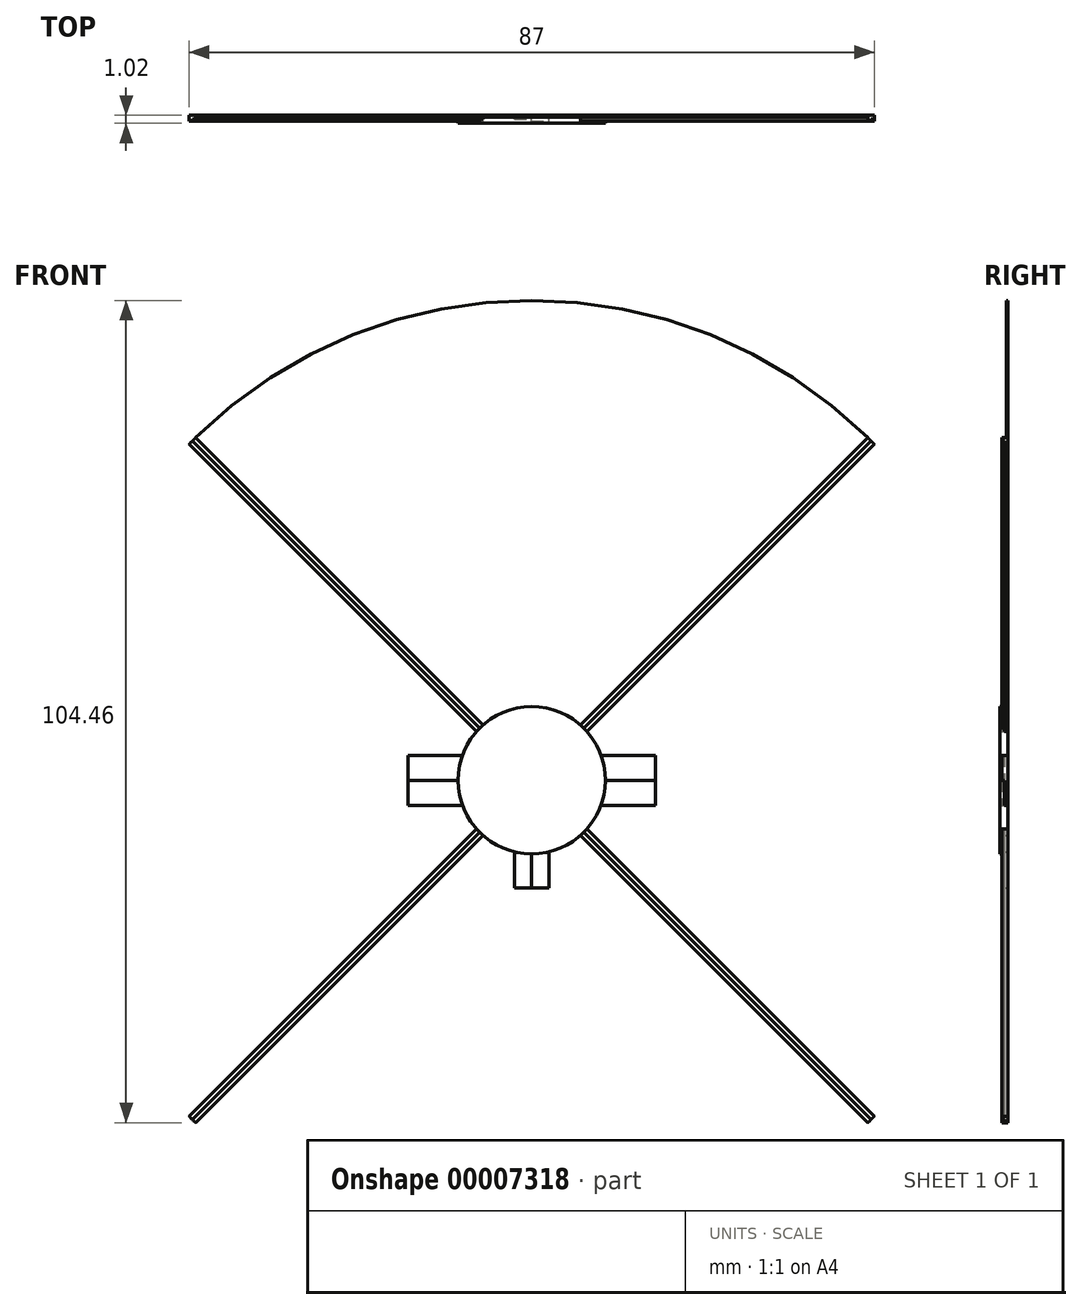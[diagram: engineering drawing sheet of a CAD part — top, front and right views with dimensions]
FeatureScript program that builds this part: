
annotation { "Feature Type Name" : "Feature", "Feature Type Description" : "" }
export const myFeature = defineFeature(function(context is Context, id is Id, definition is map)
    precondition{}
    {
        {
            var Q0;
            Q0=qCreatedBy(makeId("Front.planeOp"),FACE);
            var sketch = newSketch(context, id + "F0", { "sketchPlane" : qUnion([Q0])});
            skCircle(sketch, "E0", {"center": v(0, 0) * mm, "radius": 60.96 * mm});
            skCircle(sketch, "E1", {"center": v(0, 0) * mm, "radius": 9.35 * mm});
            skLineSegment(sketch, "E2", {"start": v(0, 0) * mm, "end": v(0, -9.35) * mm});
            skLineSegment(sketch, "E3", {"start": v(0, -9.35) * mm, "end": v(0, -60.96) * mm});
            skCircle(sketch, "E4", {"center": v(0, -11.52) * mm, "radius": 2.17 * mm});
            skLineSegment(sketch, "E5", {"start": v(-2.17, -13.7) * mm, "end": v(0, -13.7) * mm});
            skLineSegment(sketch, "E6", {"start": v(0, -13.7) * mm, "end": v(2.17, -13.7) * mm});
            skLineSegment(sketch, "E7", {"start": v(2.17, -13.7) * mm, "end": v(2.17, -9.1) * mm});
            skLineSegment(sketch, "E8", {"start": v(-2.17, -9.1) * mm, "end": v(-2.17, -13.7) * mm});
            skLineSegment(sketch, "E9", {"start": v(-8.8, 3.17) * mm, "end": v(-15.7, 3.17) * mm});
            skLineSegment(sketch, "E10", {"start": v(-15.7, 3.17) * mm, "end": v(-15.7, 0) * mm});
            skLineSegment(sketch, "E11", {"start": v(-15.7, 0) * mm, "end": v(-15.7, -3.18) * mm});
            skLineSegment(sketch, "E12", {"start": v(-15.7, -3.18) * mm, "end": v(-8.8, -3.18) * mm});
            skLineSegment(sketch, "E13", {"start": v(-15.7, 0) * mm, "end": v(0, 0) * mm});
            skLineSegment(sketch, "E14.MirrorCS", {"start": v(15.7, 0) * mm, "end": v(0, 0) * mm});
            skLineSegment(sketch, "E15.MirrorCS", {"start": v(8.8, 3.18) * mm, "end": v(15.7, 3.18) * mm});
            skLineSegment(sketch, "E16.MirrorCS", {"start": v(15.7, 3.18) * mm, "end": v(15.7, 0) * mm});
            skLineSegment(sketch, "E17.MirrorCS", {"start": v(15.7, 0) * mm, "end": v(15.7, -3.17) * mm});
            skLineSegment(sketch, "E18.MirrorCS", {"start": v(15.7, -3.17) * mm, "end": v(8.8, -3.17) * mm});
            skLineSegment(sketch, "E19", {"start": v(6.6, -6.6) * mm, "end": v(43.1, -43.1) * mm});
            skLineSegment(sketch, "E20.MirrorCS", {"start": v(-6.6, -6.6) * mm, "end": v(-43.1, -43.1) * mm});
            skLineSegment(sketch, "E21.MirrorCS", {"start": v(-6.6, 6.6) * mm, "end": v(-43.1, 43.1) * mm});
            skLineSegment(sketch, "E22.MirrorCS", {"start": v(6.6, 6.6) * mm, "end": v(43.1, 43.1) * mm});
            skLineSegment(sketch, "E23", {"start": v(-6.2, 7) * mm, "end": v(-42.7, 43.5) * mm});
            skLineSegment(sketch, "E24.MirrorCS", {"start": v(-7, 6.2) * mm, "end": v(-43.5, 42.7) * mm});
            skLineSegment(sketch, "E25.MirrorCS", {"start": v(6.2, 7) * mm, "end": v(42.7, 43.5) * mm});
            skLineSegment(sketch, "E26.MirrorCS", {"start": v(7, 6.2) * mm, "end": v(43.5, 42.7) * mm});
            skLineSegment(sketch, "E27.MirrorCS", {"start": v(-6.2, -7) * mm, "end": v(-42.7, -43.5) * mm});
            skLineSegment(sketch, "E28.MirrorCS", {"start": v(-7, -6.2) * mm, "end": v(-43.5, -42.7) * mm});
            skLineSegment(sketch, "E29.MirrorCS", {"start": v(7, -6.2) * mm, "end": v(43.5, -42.7) * mm});
            skLineSegment(sketch, "E30.MirrorCS", {"start": v(6.2, -7) * mm, "end": v(42.7, -43.5) * mm});
            skSolve(sketch);
        }
        {
            var Q0;
            {var subQ0=sQuery(id+"F0.wireOp",EDGE,"E23");Q0=makeQuery(id+"F0.imprint","IMPRINT",FACE,{"disambiguationData":[TD([[makeQuery(id+"F0.imprint","IMPRINT",EDGE,{"derivedFrom":subQ0}),-1.0]])]});}
            var Q1;
            {var subQ0=sQuery(id+"F0.wireOp",EDGE,"E15.MirrorCS");Q1=makeQuery(id+"F0.imprint","IMPRINT",FACE,{"disambiguationData":[TD([[makeQuery(id+"F0.imprint","IMPRINT",EDGE,{"derivedFrom":subQ0}),1.0]])]});}
            var Q2;
            {var subQ0=sQuery(id+"F0.wireOp",EDGE,"E5");Q2=makeQuery(id+"F0.imprint","IMPRINT",FACE,{"disambiguationData":[TD([[makeQuery(id+"F0.imprint","IMPRINT",EDGE,{"derivedFrom":subQ0}),-1.0]])]});}
            var Q3;
            {var subQ0=sQuery(id+"F0.wireOp",EDGE,"E6");Q3=makeQuery(id+"F0.imprint","IMPRINT",FACE,{"disambiguationData":[TD([[makeQuery(id+"F0.imprint","IMPRINT",EDGE,{"derivedFrom":subQ0}),-1.0]])]});}
            var Q4;
            {var subQ0=sQuery(id+"F0.wireOp",EDGE,"E9");Q4=makeQuery(id+"F0.imprint","IMPRINT",FACE,{"disambiguationData":[TD([[makeQuery(id+"F0.imprint","IMPRINT",EDGE,{"derivedFrom":subQ0}),-1.0]])]});}
            extrude(context, id + "F1", {"entities" : qUnion([Q0, Q1, Q2, Q3, Q4]), "depth" : 0.25 * mm});
        }
        {
            var Q0;
            {var subQ0=sQuery(id+"F0.wireOp",EDGE,"E21.MirrorCS");Q0=makeQuery(id+"F0.imprint","IMPRINT",FACE,{"disambiguationData":[TD([[makeQuery(id+"F0.imprint","IMPRINT",EDGE,{"derivedFrom":subQ0}),-1.0]])]});}
            var Q1;
            {var subQ0=sQuery(id+"F0.wireOp",EDGE,"E22.MirrorCS");Q1=makeQuery(id+"F0.imprint","IMPRINT",FACE,{"disambiguationData":[TD([[makeQuery(id+"F0.imprint","IMPRINT",EDGE,{"derivedFrom":subQ0}),-1.0]])]});}
            var Q2;
            {var subQ4=sQuery(id+"F0.wireOp",EDGE,"E17.MirrorCS");Q2=makeQuery(id+"F0.imprint","IMPRINT",FACE,{"disambiguationData":[TD([[makeQuery(id+"F0.imprint","IMPRINT",EDGE,{"derivedFrom":subQ4}),-1.0]])]});}
            var Q3;
            {var subQ0=sQuery(id+"F0.wireOp",EDGE,"E19");Q3=makeQuery(id+"F0.imprint","IMPRINT",FACE,{"disambiguationData":[TD([[makeQuery(id+"F0.imprint","IMPRINT",EDGE,{"derivedFrom":subQ0}),-1.0]])]});}
            var Q4;
            {var subQ0=sQuery(id+"F0.wireOp",EDGE,"E5");Q4=makeQuery(id+"F0.imprint","IMPRINT",FACE,{"disambiguationData":[TD([[makeQuery(id+"F0.imprint","IMPRINT",EDGE,{"derivedFrom":subQ0}),1.0]])]});}
            var Q5;
            {var subQ0=sQuery(id+"F0.wireOp",EDGE,"E4");var subQ4=makeQuery(id+"F0.imprint","INTERSECT",VERTEX,{"derivedFrom":[subQ0,sQuery(id+"F0.wireOp",EDGE,"E8")]});Q5=makeQuery(id+"F0.imprint","IMPRINT",FACE,{"disambiguationData":[TD([[makeQuery(id+"F0.imprint","IMPRINT",EDGE,{"disambiguationData":[TD([[subQ4,1.0]])],"derivedFrom":subQ0}),1.0]])]});}
            var Q6;
            {var subQ1=sQuery(id+"F0.wireOp",EDGE,"E1");var subQ3=sQuery(id+"F0.wireOp",EDGE,"E8");var subQ4=makeQuery(id+"F0.imprint","INTERSECT",VERTEX,{"derivedFrom":[subQ1,subQ3]});Q6=makeQuery(id+"F0.imprint","IMPRINT",FACE,{"disambiguationData":[TD([[makeQuery(id+"F0.imprint","IMPRINT",EDGE,{"disambiguationData":[TD([[subQ4,-1.0]])],"derivedFrom":subQ3}),1.0]])]});}
            var Q7;
            {var subQ0=sQuery(id+"F0.wireOp",EDGE,"E20.MirrorCS");Q7=makeQuery(id+"F0.imprint","IMPRINT",FACE,{"disambiguationData":[TD([[makeQuery(id+"F0.imprint","IMPRINT",EDGE,{"derivedFrom":subQ0}),-1.0]])]});}
            var Q8;
            {var subQ0=sQuery(id+"F0.wireOp",EDGE,"E9");Q8=makeQuery(id+"F0.imprint","IMPRINT",FACE,{"disambiguationData":[TD([[makeQuery(id+"F0.imprint","IMPRINT",EDGE,{"derivedFrom":subQ0}),1.0]])]});}
            extrude(context, id + "F2", {"entities" : qUnion([Q0, Q1, Q2, Q3, Q4, Q5, Q6, Q7, Q8]), "operationType" : NewBodyOperationType.ADD, "depth" : 0.5 * mm});
        }
        {
            var Q0;
            {var subQ0=sQuery(id+"F0.wireOp",EDGE,"E21.MirrorCS");Q0=makeQuery(id+"F0.imprint","IMPRINT",FACE,{"disambiguationData":[TD([[makeQuery(id+"F0.imprint","IMPRINT",EDGE,{"derivedFrom":subQ0}),1.0]])]});}
            var Q1;
            {var subQ0=sQuery(id+"F0.wireOp",EDGE,"E22.MirrorCS");Q1=makeQuery(id+"F0.imprint","IMPRINT",FACE,{"disambiguationData":[TD([[makeQuery(id+"F0.imprint","IMPRINT",EDGE,{"derivedFrom":subQ0}),1.0]])]});}
            var Q2;
            {var subQ0=sQuery(id+"F0.wireOp",EDGE,"E15.MirrorCS");Q2=makeQuery(id+"F0.imprint","IMPRINT",FACE,{"disambiguationData":[TD([[makeQuery(id+"F0.imprint","IMPRINT",EDGE,{"derivedFrom":subQ0}),-1.0]])]});}
            var Q3;
            {var subQ0=sQuery(id+"F0.wireOp",EDGE,"E19");Q3=makeQuery(id+"F0.imprint","IMPRINT",FACE,{"disambiguationData":[TD([[makeQuery(id+"F0.imprint","IMPRINT",EDGE,{"derivedFrom":subQ0}),1.0]])]});}
            var Q4;
            {var subQ1=sQuery(id+"F0.wireOp",EDGE,"E1");var subQ3=sQuery(id+"F0.wireOp",EDGE,"E7");var subQ4=makeQuery(id+"F0.imprint","INTERSECT",VERTEX,{"derivedFrom":[subQ1,subQ3]});Q4=makeQuery(id+"F0.imprint","IMPRINT",FACE,{"disambiguationData":[TD([[makeQuery(id+"F0.imprint","IMPRINT",EDGE,{"disambiguationData":[TD([[subQ4,1.0]])],"derivedFrom":subQ3}),1.0]])]});}
            var Q5;
            {var subQ0=sQuery(id+"F0.wireOp",EDGE,"E4");var subQ4=makeQuery(id+"F0.imprint","INTERSECT",VERTEX,{"derivedFrom":[subQ0,sQuery(id+"F0.wireOp",EDGE,"E7")]});Q5=makeQuery(id+"F0.imprint","IMPRINT",FACE,{"disambiguationData":[TD([[makeQuery(id+"F0.imprint","IMPRINT",EDGE,{"disambiguationData":[TD([[subQ4,-1.0]])],"derivedFrom":subQ0}),1.0]])]});}
            var Q6;
            {var subQ0=sQuery(id+"F0.wireOp",EDGE,"E6");Q6=makeQuery(id+"F0.imprint","IMPRINT",FACE,{"disambiguationData":[TD([[makeQuery(id+"F0.imprint","IMPRINT",EDGE,{"derivedFrom":subQ0}),1.0]])]});}
            var Q7;
            {var subQ0=sQuery(id+"F0.wireOp",EDGE,"E20.MirrorCS");Q7=makeQuery(id+"F0.imprint","IMPRINT",FACE,{"disambiguationData":[TD([[makeQuery(id+"F0.imprint","IMPRINT",EDGE,{"derivedFrom":subQ0}),1.0]])]});}
            var Q8;
            {var subQ4=sQuery(id+"F0.wireOp",EDGE,"E11");Q8=makeQuery(id+"F0.imprint","IMPRINT",FACE,{"disambiguationData":[TD([[makeQuery(id+"F0.imprint","IMPRINT",EDGE,{"derivedFrom":subQ4}),1.0]])]});}
            extrude(context, id + "F3", {"entities" : qUnion([Q0, Q1, Q2, Q3, Q4, Q5, Q6, Q7, Q8]), "operationType" : NewBodyOperationType.ADD, "depth" : 0.76 * mm});
        }
        {
            var Q0;
            {var subQ0=sQuery(id+"F0.wireOp",EDGE,"E1");var subQ10=makeQuery(id+"F0.imprint","INTERSECT",VERTEX,{"derivedFrom":[subQ0,sQuery(id+"F0.wireOp",EDGE,"E15.MirrorCS")]});Q0=makeQuery(id+"F0.imprint","IMPRINT",FACE,{"disambiguationData":[TD([[makeQuery(id+"F0.imprint","IMPRINT",EDGE,{"disambiguationData":[TD([[subQ10,1.0]])],"derivedFrom":subQ0}),1.0]])]});}
            var Q1;
            {var subQ5=sQuery(id+"F0.wireOp",EDGE,"E2");Q1=makeQuery(id+"F0.imprint","IMPRINT",FACE,{"disambiguationData":[TD([[makeQuery(id+"F0.imprint","IMPRINT",EDGE,{"derivedFrom":subQ5}),1.0]])]});}
            var Q2;
            {var subQ5=sQuery(id+"F0.wireOp",EDGE,"E2");Q2=makeQuery(id+"F0.imprint","IMPRINT",FACE,{"disambiguationData":[TD([[makeQuery(id+"F0.imprint","IMPRINT",EDGE,{"derivedFrom":subQ5}),-1.0]])]});}
            extrude(context, id + "F4", {"entities" : qUnion([Q0, Q1, Q2]), "operationType" : NewBodyOperationType.ADD, "depth" : 1.02 * mm});
        }
    });
